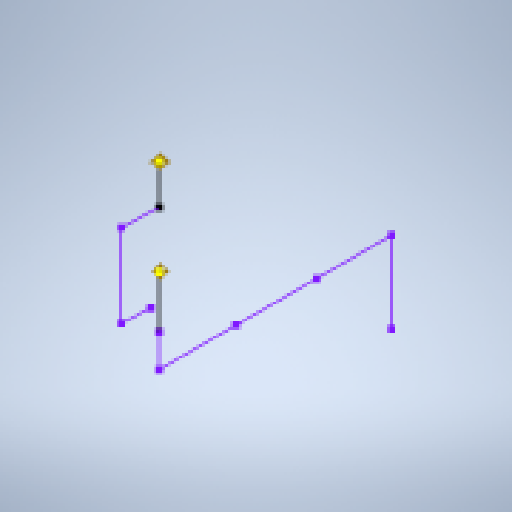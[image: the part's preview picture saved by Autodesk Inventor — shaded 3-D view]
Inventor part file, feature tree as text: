
AUTODESK INVENTOR PART (.ipt)
format: ipt  version: 2025 (Build 290162000, 162)  size: 197,120 bytes
history: native  units: in
note: dims shown in document units (in); Inventor stores cm internally (conversion verified against a paired STEP export)
features: other x10, plane x3, sketch x1
ambient origin geometry x8: Origin, YZ Plane, XZ Plane, XY Plane, X Axis, Y Axis, Z Axis, Center Point
feature tree (14):
  other  "{4D39D5F1-0985-4783-AA5A-FC16C288418C}"
  other  "Work Point3"
  plane  "Work Plane3"
  other  "Work Point4"
  other  "Work Point5"
  other  "Work Point6"
  other  "Work Point7"
  other  "Work Point8"
  other  "Work Point9"
  plane  "Work Plane4"
  other  "Work Point10"
  other  "Work Point11"
  plane  "Work Plane5"
  sketch  "3D Sketch1"
